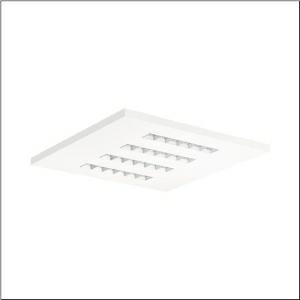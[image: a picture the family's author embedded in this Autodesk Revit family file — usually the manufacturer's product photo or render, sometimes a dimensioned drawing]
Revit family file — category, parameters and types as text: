
# Revit family: silica_r__21_square_51mx6mds34w_a914
name_source: partatom
category: Lighting Fixtures
units: mm (PartAtom-declared; Revit-internal decimal feet)

## family parameters
Cut with Voids When Loaded = No
Host = Face
Light Source = No
Part Type = Normal
Room Calculation Point = No
Round Connector Dimension = Use Diameter
Shared = No

## types (1)
- --- (1 x LED, 4600 lm, 29.2 W, 3000K)
    Apparent Load = 29 VA
    CIE Flux Codes = 83 98 100 100 100
    Color Rendering = 80
    Color Temperature = 3000K
    Default Elevation = 1800 mm
    Description = Silica® 21 Square, office luminaire, primary light control with lens, of PMMA, primary anti-glare with reflector, of PC, white, CAT 2 (L<= 3000cd/m²), light emission: direct distribution, primary light characteristic: symmetric, installation type: lay-in mounting, LED, rated luminous flux: 4.600lm, luminous efficacy: 158lm/W, light colour: 830, colour temperature: 3000K, control gear: DALI 2, with terminal, 5-pole, mains connection: 220..240V, AC, 50/60Hz, rated input power: 29.2W, luminaire housing, of sheet steel, coated, traffic white (RAL 9016), module: M600, length: 597mm, width: 597mm, height: 33mm, protection rating (complete): IP20, insulation class (complete): insulation class I (protective earthing), certification: CE, ENEC, VDE, permissible operating ambient temperature: -20..+40°C, standard: EN 50419, packaging unit: 1 piece
    Height = 0 mm  [stored 0 ft]
    Lamp = 1 x LED
    Lamp Light Flux = 4600 lm
    Lamp Power = 29.2 W
    Lamp count = 1
    Length = 597 mm
    Luminous efficacy = 158 lm/W
    Manufacturer = Siteco
    ModVariant = No
    Model = 51MX6MDS34W
    Mounting Place = Ceiling
    Mounting Type = Recessed
    Number of Poles = 1
    OnlyDefault = Yes
    Power Factor = 1
    Product Name = Silica® 21 Square
    Product group = office luminaire | ceiling recessed
    ProductGroupID = 401
    Protection Class = Protection class I
    Protection Degree = IP 20
    RLX_Detail_Level = 1
    RLX_Emergency_Light_Flux = 0 lm
    RLX_Emergency_Type = 0
    RLX_Emergency_Type_DB = No
    RlxData = <blob elided: 18541 chars, md5=ac77e01c>
    Socket = socket
    Standby Power = 0 W
    System Light Flux = 4600 lm
    System Power = 29 W
    Type Comments = factory setting: luminous flux: 100 % | dim-lin: 254 | 393 mA
    Type Image = l_1275220.jpg
    URL = http://relux.com
    VarID = @adj_083824
    Voltage = 0 V
    Weight = 0.00 kg
    Width = 597 mm

note: [stored X ft] marks values corroborated as IEEE doubles in the binary element streams (Revit-internal decimal feet)

## geometry (parser evidence)
native form markers: Blend x4, Sweep x11
no freeform markers — native parametric forms only
